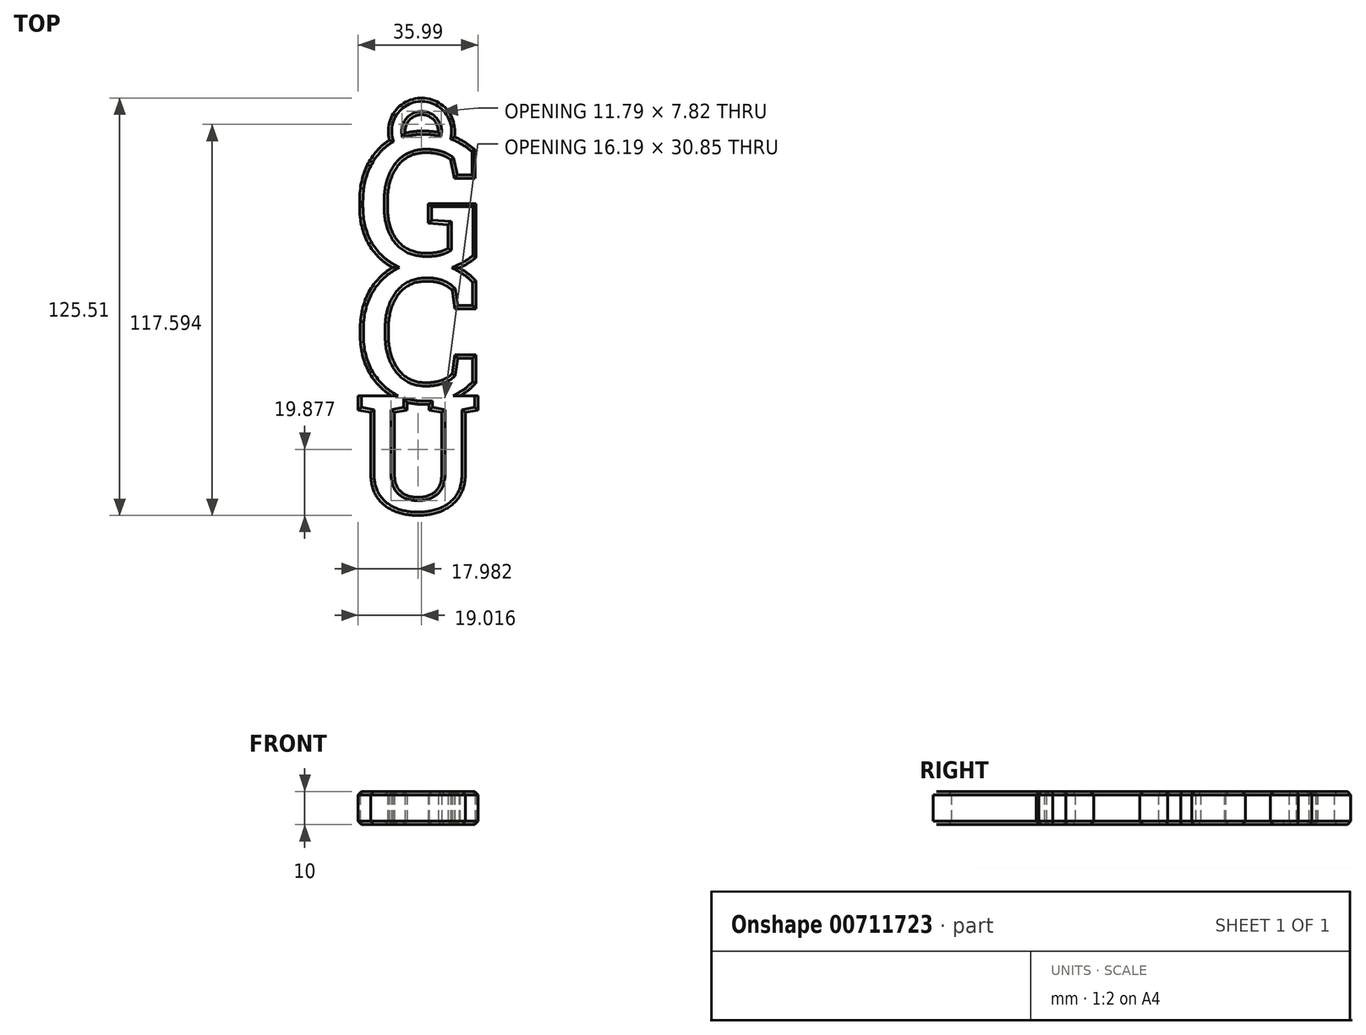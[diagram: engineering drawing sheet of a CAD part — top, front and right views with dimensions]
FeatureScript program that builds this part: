
annotation { "Feature Type Name" : "Feature", "Feature Type Description" : "" }
export const myFeature = defineFeature(function(context is Context, id is Id, definition is map)
    precondition{}
    {
        {
            var Q0;
            Q0=qCreatedBy(makeId("Top.planeOp"),FACE);
            var sketch = newSketch(context, id + "F0", { "sketchPlane" : qUnion([Q0])});
            skText(sketch, "E0", { "text": "G", "fontName": "RobotoSlab-Bold.ttf"});
            skText(sketch, "E1", { "text": "C", "fontName": "RobotoSlab-Bold.ttf"});
            skText(sketch, "E2", { "text": "U", "fontName": "RobotoSlab-Bold.ttf"});
            skCircle(sketch, "E3", {"center": v(0, 51.5) * mm, "radius": 10 * mm});
            skCircle(sketch, "E4", {"center": v(0, 51.5) * mm, "radius": 5 * mm});
            const initialGuessF0  = {"E0": [-0.02, 0.00902, 1, 0, 0.04248], "E1": [-0.02, -0.03003, 1, 0, 0.04292], "E2": [-0.02, -0.0635, 1, 0, 0.0359]};
            skSetInitialGuess(sketch, initialGuessF0);
            skSolve(sketch);
        }
        {
            var Q0;
            {var subQ11=sQuery(id+"F0.wireOp",EDGE,"E0.sketch_text.stroke-3");Q0=makeQuery(id+"F0.imprint","IMPRINT",FACE,{"disambiguationData":[TD([[makeQuery(id+"F0.imprint","IMPRINT",EDGE,{"derivedFrom":subQ11}),-1.0]])]});}
            var Q1;
            {var subQ7=sQuery(id+"F0.wireOp",EDGE,"E0.sketch_text.stroke-13");Q1=makeQuery(id+"F0.imprint","IMPRINT",FACE,{"disambiguationData":[TD([[makeQuery(id+"F0.imprint","IMPRINT",EDGE,{"derivedFrom":subQ7}),-1.0]])]});}
            var Q2;
            {var subQ0=sQuery(id+"F0.wireOp",EDGE,"E3");var subQ1=sQuery(id+"F0.wireOp",EDGE,"E0.sketch_text.stroke-6");var subQ2=makeQuery(id+"F0.imprint","INTERSECT",VERTEX,{"derivedFrom":[subQ1,subQ0]});Q2=makeQuery(id+"F0.imprint","IMPRINT",FACE,{"disambiguationData":[TD([[makeQuery(id+"F0.imprint","IMPRINT",EDGE,{"disambiguationData":[TD([[subQ2,-1.0]])],"derivedFrom":subQ1}),1.0]])]});}
            var Q3;
            {var subQ0=sQuery(id+"F0.wireOp",EDGE,"E0.sketch_text.stroke-7");var subQ1=sQuery(id+"F0.wireOp",EDGE,"E0.sketch_text.stroke-6");var subQ2=makeQuery(id+"F0.imprint","INTERSECT",VERTEX,{"derivedFrom":[subQ1,subQ0]});Q3=makeQuery(id+"F0.imprint","IMPRINT",FACE,{"disambiguationData":[TD([[makeQuery(id+"F0.imprint","IMPRINT",EDGE,{"disambiguationData":[TD([[subQ2,1.0]])],"derivedFrom":subQ1}),-1.0]])]});}
            var Q4;
            {var subQ6=sQuery(id+"F0.wireOp",EDGE,"E0.sketch_text.stroke-9");Q4=makeQuery(id+"F0.imprint","IMPRINT",FACE,{"disambiguationData":[TD([[makeQuery(id+"F0.imprint","IMPRINT",EDGE,{"derivedFrom":subQ6}),-1.0]])]});}
            var Q5;
            {var subQ4=sQuery(id+"F0.wireOp",EDGE,"E0.sketch_text.stroke-1");Q5=makeQuery(id+"F0.imprint","IMPRINT",FACE,{"disambiguationData":[TD([[makeQuery(id+"F0.imprint","IMPRINT",EDGE,{"derivedFrom":subQ4}),-1.0]])]});}
            var Q6;
            {var subQ12=sQuery(id+"F0.wireOp",EDGE,"E0.sketch_text.stroke-1");Q6=makeQuery(id+"F0.imprint","IMPRINT",FACE,{"disambiguationData":[TD([[makeQuery(id+"F0.imprint","IMPRINT",EDGE,{"derivedFrom":subQ12}),1.0]])]});}
            var Q7;
            {var subQ13=sQuery(id+"F0.wireOp",EDGE,"E2.sketch_text.stroke-1");Q7=makeQuery(id+"F0.imprint","IMPRINT",FACE,{"disambiguationData":[TD([[makeQuery(id+"F0.imprint","IMPRINT",EDGE,{"derivedFrom":subQ13}),-1.0]])]});}
            var Q8;
            {var subQ0=sQuery(id+"F0.wireOp",EDGE,"E1.sketch_text.stroke-15");var subQ1=sQuery(id+"F0.wireOp",EDGE,"E1.sketch_text.stroke-14");var subQ2=makeQuery(id+"F0.imprint","INTERSECT",VERTEX,{"derivedFrom":[subQ1,subQ0]});Q8=makeQuery(id+"F0.imprint","IMPRINT",FACE,{"disambiguationData":[TD([[makeQuery(id+"F0.imprint","IMPRINT",EDGE,{"disambiguationData":[TD([[subQ2,1.0]])],"derivedFrom":subQ1}),-1.0]])]});}
            var Q9;
            {var subQ5=sQuery(id+"F0.wireOp",EDGE,"E2.sketch_text.stroke-23");Q9=makeQuery(id+"F0.imprint","IMPRINT",FACE,{"disambiguationData":[TD([[makeQuery(id+"F0.imprint","IMPRINT",EDGE,{"derivedFrom":subQ5}),-1.0]])]});}
            extrude(context, id + "F1", {"entities" : qUnion([Q0, Q1, Q2, Q3, Q4, Q5, Q6, Q7, Q8, Q9]), "depth" : 10 * mm, "offsetDistance" : 25 * mm});
        }
        {
            var Q0;
            Q0=makeQuery(id+"F1.opExtrude","CAP_EDGE",EDGE,{"disambiguationData":[OSD([sQuery(id+"F0.wireOp",EDGE,"E0.sketch_text.stroke-2")])],"isStart":false});
            var Q1;
            Q1=makeQuery(id+"F1.opExtrude","CAP_EDGE",EDGE,{"disambiguationData":[OSD([sQuery(id+"F0.wireOp",EDGE,"E0.sketch_text.stroke-3")])],"isStart":false});
            var Q2;
            Q2=makeQuery(id+"F1.opExtrude","CAP_EDGE",EDGE,{"disambiguationData":[OSD([sQuery(id+"F0.wireOp",EDGE,"E3")])],"isStart":false});
            var Q3;
            Q3=makeQuery(id+"F1.opExtrude","CAP_EDGE",EDGE,{"disambiguationData":[OSD([sQuery(id+"F0.wireOp",EDGE,"E0.sketch_text.stroke-8")])],"isStart":false});
            var Q4;
            Q4=makeQuery(id+"F1.opExtrude","CAP_EDGE",EDGE,{"disambiguationData":[OSD([sQuery(id+"F0.wireOp",EDGE,"E0.sketch_text.stroke-9")])],"isStart":false});
            var Q5;
            Q5=makeQuery(id+"F1.opExtrude","CAP_EDGE",EDGE,{"disambiguationData":[OSD([sQuery(id+"F0.wireOp",EDGE,"E0.sketch_text.stroke-24")])],"isStart":false});
            var Q6;
            Q6=makeQuery(id+"F1.opExtrude","CAP_EDGE",EDGE,{"disambiguationData":[OSD([sQuery(id+"F0.wireOp",EDGE,"E0.sketch_text.stroke-10")])],"isStart":false});
            var Q7;
            Q7=makeQuery(id+"F1.opExtrude","CAP_EDGE",EDGE,{"disambiguationData":[OSD([sQuery(id+"F0.wireOp",EDGE,"E0.sketch_text.stroke-11")])],"isStart":false});
            var Q8;
            Q8=makeQuery(id+"F1.opExtrude","CAP_EDGE",EDGE,{"disambiguationData":[OSD([sQuery(id+"F0.wireOp",EDGE,"E0.sketch_text.stroke-13")])],"isStart":false});
            var Q9;
            Q9=makeQuery(id+"F1.opExtrude","CAP_EDGE",EDGE,{"disambiguationData":[OSD([sQuery(id+"F0.wireOp",EDGE,"E0.sketch_text.stroke-21")])],"isStart":false});
            var Q10;
            Q10=makeQuery(id+"F1.opExtrude","CAP_EDGE",EDGE,{"disambiguationData":[OSD([sQuery(id+"F0.wireOp",EDGE,"E0.sketch_text.stroke-22")])],"isStart":false});
            var Q11;
            Q11=makeQuery(id+"F1.opExtrude","CAP_EDGE",EDGE,{"disambiguationData":[OSD([sQuery(id+"F0.wireOp",EDGE,"E0.sketch_text.stroke-23")])],"isStart":false});
            var Q12;
            Q12=makeQuery(id+"F1.opExtrude","CAP_EDGE",EDGE,{"disambiguationData":[OSD([sQuery(id+"F0.wireOp",EDGE,"E0.sketch_text.stroke-25")])],"isStart":false});
            var Q13;
            Q13=makeQuery(id+"F1.opExtrude","CAP_EDGE",EDGE,{"disambiguationData":[OSD([sQuery(id+"F0.wireOp",EDGE,"E0.sketch_text.stroke-0")])],"isStart":false});
            var Q14;
            Q14=makeQuery(id+"F1.opExtrude","CAP_EDGE",EDGE,{"disambiguationData":[OSD([sQuery(id+"F0.wireOp",EDGE,"E1.sketch_text.stroke-22")])],"isStart":false});
            var Q15;
            Q15=makeQuery(id+"F1.opExtrude","CAP_EDGE",EDGE,{"disambiguationData":[OSD([sQuery(id+"F0.wireOp",EDGE,"E1.sketch_text.stroke-23")])],"isStart":false});
            var Q16;
            Q16=makeQuery(id+"F1.opExtrude","CAP_EDGE",EDGE,{"disambiguationData":[OSD([sQuery(id+"F0.wireOp",EDGE,"E1.sketch_text.stroke-0")])],"isStart":false});
            var Q17;
            Q17=makeQuery(id+"F1.opExtrude","CAP_EDGE",EDGE,{"disambiguationData":[OSD([sQuery(id+"F0.wireOp",EDGE,"E1.sketch_text.stroke-1")])],"isStart":false});
            var Q18;
            Q18=makeQuery(id+"F1.opExtrude","CAP_EDGE",EDGE,{"disambiguationData":[OSD([sQuery(id+"F0.wireOp",EDGE,"E1.sketch_text.stroke-2")])],"isStart":false});
            var Q19;
            Q19=makeQuery(id+"F1.opExtrude","CAP_EDGE",EDGE,{"disambiguationData":[OSD([sQuery(id+"F0.wireOp",EDGE,"E1.sketch_text.stroke-12")])],"isStart":false});
            var Q20;
            Q20=makeQuery(id+"F1.opExtrude","CAP_EDGE",EDGE,{"disambiguationData":[OSD([sQuery(id+"F0.wireOp",EDGE,"E1.sketch_text.stroke-11")])],"isStart":false});
            var Q21;
            Q21=makeQuery(id+"F1.opExtrude","CAP_EDGE",EDGE,{"disambiguationData":[OSD([sQuery(id+"F0.wireOp",EDGE,"E1.sketch_text.stroke-13")])],"isStart":false});
            var Q22;
            Q22=makeQuery(id+"F1.opExtrude","CAP_EDGE",EDGE,{"disambiguationData":[OSD([sQuery(id+"F0.wireOp",EDGE,"E1.sketch_text.stroke-14")])],"isStart":false});
            var Q23;
            Q23=makeQuery(id+"F1.opExtrude","CAP_EDGE",EDGE,{"disambiguationData":[OSD([sQuery(id+"F0.wireOp",EDGE,"E2.sketch_text.stroke-11")])],"isStart":false});
            var Q24;
            Q24=makeQuery(id+"F1.opExtrude","CAP_EDGE",EDGE,{"disambiguationData":[OSD([sQuery(id+"F0.wireOp",EDGE,"E2.sketch_text.stroke-12")])],"isStart":false});
            var Q25;
            Q25=makeQuery(id+"F1.opExtrude","CAP_EDGE",EDGE,{"disambiguationData":[OSD([sQuery(id+"F0.wireOp",EDGE,"E2.sketch_text.stroke-13")])],"isStart":false});
            var Q26;
            Q26=makeQuery(id+"F1.opExtrude","CAP_EDGE",EDGE,{"disambiguationData":[OSD([sQuery(id+"F0.wireOp",EDGE,"E1.sketch_text.stroke-17")])],"isStart":false});
            var Q27;
            Q27=makeQuery(id+"F1.opExtrude","CAP_EDGE",EDGE,{"disambiguationData":[OSD([sQuery(id+"F0.wireOp",EDGE,"E2.sketch_text.stroke-20")])],"isStart":false});
            var Q28;
            Q28=makeQuery(id+"F1.opExtrude","CAP_EDGE",EDGE,{"disambiguationData":[OSD([sQuery(id+"F0.wireOp",EDGE,"E2.sketch_text.stroke-19")])],"isStart":false});
            var Q29;
            Q29=makeQuery(id+"F1.opExtrude","CAP_EDGE",EDGE,{"disambiguationData":[OSD([sQuery(id+"F0.wireOp",EDGE,"E2.sketch_text.stroke-13")])],"isStart":true});
            var Q30;
            Q30=makeQuery(id+"F1.opExtrude","CAP_EDGE",EDGE,{"disambiguationData":[OSD([sQuery(id+"F0.wireOp",EDGE,"E2.sketch_text.stroke-7")])],"isStart":true});
            var Q31;
            Q31=makeQuery(id+"F1.opExtrude","CAP_EDGE",EDGE,{"disambiguationData":[OSD([sQuery(id+"F0.wireOp",EDGE,"E2.sketch_text.stroke-7")])],"isStart":false});
            var Q32;
            Q32=makeQuery(id+"F1.opExtrude","CAP_EDGE",EDGE,{"disambiguationData":[OSD([sQuery(id+"F0.wireOp",EDGE,"E2.sketch_text.stroke-8")])],"isStart":false});
            var Q33;
            {var subQ0=sQuery(id+"F0.wireOp",EDGE,"E1.sketch_text.stroke-16");Q33=makeQuery(id+"F1.opExtrude","CAP_EDGE",EDGE,{"disambiguationData":[OSD([subQ0]),TDD([makeQuery(id+"F0.imprint","IMPRINT",EDGE,{"disambiguationData":[TD([[makeQuery(id+"F0.imprint","INTERSECT",VERTEX,{"derivedFrom":[sQuery(id+"F0.wireOp",EDGE,"E1.sketch_text.stroke-15"),subQ0]}),-1.0]])],"derivedFrom":subQ0})])],"isStart":false});}
            var Q34;
            Q34=makeQuery(id+"F1.opExtrude","CAP_EDGE",EDGE,{"disambiguationData":[OSD([sQuery(id+"F0.wireOp",EDGE,"E2.sketch_text.stroke-1")])],"isStart":false});
            var Q35;
            Q35=makeQuery(id+"F1.opExtrude","CAP_EDGE",EDGE,{"disambiguationData":[OSD([sQuery(id+"F0.wireOp",EDGE,"E2.sketch_text.stroke-8")])],"isStart":true});
            var Q36;
            {var subQ0=sQuery(id+"F0.wireOp",EDGE,"E1.sketch_text.stroke-16");Q36=makeQuery(id+"F1.opExtrude","CAP_EDGE",EDGE,{"disambiguationData":[OSD([subQ0]),TDD([makeQuery(id+"F0.imprint","IMPRINT",EDGE,{"disambiguationData":[TD([[makeQuery(id+"F0.imprint","INTERSECT",VERTEX,{"derivedFrom":[sQuery(id+"F0.wireOp",EDGE,"E1.sketch_text.stroke-15"),subQ0]}),-1.0]])],"derivedFrom":subQ0})])],"isStart":true});}
            var Q37;
            Q37=makeQuery(id+"F1.opExtrude","CAP_EDGE",EDGE,{"disambiguationData":[OSD([sQuery(id+"F0.wireOp",EDGE,"E1.sketch_text.stroke-8")])],"isStart":true});
            var Q38;
            Q38=makeQuery(id+"F1.opExtrude","CAP_EDGE",EDGE,{"disambiguationData":[OSD([sQuery(id+"F0.wireOp",EDGE,"E2.sketch_text.stroke-12")])],"isStart":true});
            var Q39;
            Q39=makeQuery(id+"F1.opExtrude","CAP_EDGE",EDGE,{"disambiguationData":[OSD([sQuery(id+"F0.wireOp",EDGE,"E2.sketch_text.stroke-11")])],"isStart":true});
            var Q40;
            Q40=makeQuery(id+"F1.opExtrude","CAP_EDGE",EDGE,{"disambiguationData":[OSD([sQuery(id+"F0.wireOp",EDGE,"E2.sketch_text.stroke-19")])],"isStart":true});
            var Q41;
            Q41=makeQuery(id+"F1.opExtrude","CAP_EDGE",EDGE,{"disambiguationData":[OSD([sQuery(id+"F0.wireOp",EDGE,"E2.sketch_text.stroke-20")])],"isStart":true});
            var Q42;
            Q42=makeQuery(id+"F1.opExtrude","CAP_EDGE",EDGE,{"disambiguationData":[OSD([sQuery(id+"F0.wireOp",EDGE,"E1.sketch_text.stroke-17")])],"isStart":true});
            var Q43;
            Q43=makeQuery(id+"F1.opExtrude","CAP_EDGE",EDGE,{"disambiguationData":[OSD([sQuery(id+"F0.wireOp",EDGE,"E1.sketch_text.stroke-11")])],"isStart":true});
            var Q44;
            Q44=makeQuery(id+"F1.opExtrude","CAP_EDGE",EDGE,{"disambiguationData":[OSD([sQuery(id+"F0.wireOp",EDGE,"E1.sketch_text.stroke-12")])],"isStart":true});
            var Q45;
            Q45=makeQuery(id+"F1.opExtrude","CAP_EDGE",EDGE,{"disambiguationData":[OSD([sQuery(id+"F0.wireOp",EDGE,"E1.sketch_text.stroke-13")])],"isStart":true});
            var Q46;
            Q46=makeQuery(id+"F1.opExtrude","CAP_EDGE",EDGE,{"disambiguationData":[OSD([sQuery(id+"F0.wireOp",EDGE,"E1.sketch_text.stroke-14")])],"isStart":true});
            var Q47;
            Q47=makeQuery(id+"F1.opExtrude","CAP_EDGE",EDGE,{"disambiguationData":[OSD([sQuery(id+"F0.wireOp",EDGE,"E1.sketch_text.stroke-23")])],"isStart":true});
            var Q48;
            Q48=makeQuery(id+"F1.opExtrude","CAP_EDGE",EDGE,{"disambiguationData":[OSD([sQuery(id+"F0.wireOp",EDGE,"E1.sketch_text.stroke-0")])],"isStart":true});
            var Q49;
            Q49=makeQuery(id+"F1.opExtrude","CAP_EDGE",EDGE,{"disambiguationData":[OSD([sQuery(id+"F0.wireOp",EDGE,"E1.sketch_text.stroke-22")])],"isStart":true});
            var Q50;
            Q50=makeQuery(id+"F1.opExtrude","CAP_EDGE",EDGE,{"disambiguationData":[OSD([sQuery(id+"F0.wireOp",EDGE,"E0.sketch_text.stroke-0")])],"isStart":true});
            var Q51;
            Q51=makeQuery(id+"F1.opExtrude","CAP_EDGE",EDGE,{"disambiguationData":[OSD([sQuery(id+"F0.wireOp",EDGE,"E0.sketch_text.stroke-25")])],"isStart":true});
            var Q52;
            Q52=makeQuery(id+"F1.opExtrude","CAP_EDGE",EDGE,{"disambiguationData":[OSD([sQuery(id+"F0.wireOp",EDGE,"E0.sketch_text.stroke-24")])],"isStart":true});
            var Q53;
            Q53=makeQuery(id+"F1.opExtrude","CAP_EDGE",EDGE,{"disambiguationData":[OSD([sQuery(id+"F0.wireOp",EDGE,"E0.sketch_text.stroke-22")])],"isStart":true});
            var Q54;
            Q54=makeQuery(id+"F1.opExtrude","CAP_EDGE",EDGE,{"disambiguationData":[OSD([sQuery(id+"F0.wireOp",EDGE,"E0.sketch_text.stroke-21")])],"isStart":true});
            var Q55;
            Q55=makeQuery(id+"F1.opExtrude","CAP_EDGE",EDGE,{"disambiguationData":[OSD([sQuery(id+"F0.wireOp",EDGE,"E0.sketch_text.stroke-17")])],"isStart":true});
            var Q56;
            Q56=makeQuery(id+"F1.opExtrude","CAP_EDGE",EDGE,{"disambiguationData":[OSD([sQuery(id+"F0.wireOp",EDGE,"E3")])],"isStart":true});
            var Q57;
            Q57=makeQuery(id+"F1.opExtrude","CAP_EDGE",EDGE,{"disambiguationData":[OSD([sQuery(id+"F0.wireOp",EDGE,"E4")])],"isStart":true});
            var Q58;
            Q58=makeQuery(id+"F1.opExtrude","CAP_EDGE",EDGE,{"disambiguationData":[OSD([sQuery(id+"F0.wireOp",EDGE,"E0.sketch_text.stroke-7")])],"isStart":true});
            var Q59;
            Q59=makeQuery(id+"F1.opExtrude","CAP_EDGE",EDGE,{"disambiguationData":[OSD([sQuery(id+"F0.wireOp",EDGE,"E0.sketch_text.stroke-8")])],"isStart":true});
            var Q60;
            Q60=makeQuery(id+"F1.opExtrude","CAP_EDGE",EDGE,{"disambiguationData":[OSD([sQuery(id+"F0.wireOp",EDGE,"E0.sketch_text.stroke-9")])],"isStart":true});
            var Q61;
            Q61=makeQuery(id+"F1.opExtrude","CAP_EDGE",EDGE,{"disambiguationData":[OSD([sQuery(id+"F0.wireOp",EDGE,"E0.sketch_text.stroke-10")])],"isStart":true});
            var Q62;
            Q62=makeQuery(id+"F1.opExtrude","CAP_EDGE",EDGE,{"disambiguationData":[OSD([sQuery(id+"F0.wireOp",EDGE,"E0.sketch_text.stroke-11")])],"isStart":true});
            var Q63;
            {var subQ0=sQuery(id+"F0.wireOp",EDGE,"E0.sketch_text.stroke-6");Q63=makeQuery(id+"F1.opExtrude","CAP_EDGE",EDGE,{"disambiguationData":[OSD([subQ0]),TDD([makeQuery(id+"F0.imprint","IMPRINT",EDGE,{"disambiguationData":[TD([[makeQuery(id+"F0.imprint","INTERSECT",VERTEX,{"derivedFrom":[subQ0,sQuery(id+"F0.wireOp",EDGE,"E0.sketch_text.stroke-7")]}),1.0]])],"derivedFrom":subQ0})])],"isStart":false});}
            var Q64;
            Q64=makeQuery(id+"F1.opExtrude","CAP_EDGE",EDGE,{"disambiguationData":[OSD([sQuery(id+"F0.wireOp",EDGE,"E4")])],"isStart":false});
            var Q65;
            Q65=makeQuery(id+"F1.opExtrude","CAP_EDGE",EDGE,{"disambiguationData":[OSD([sQuery(id+"F0.wireOp",EDGE,"E0.sketch_text.stroke-5")])],"isStart":true});
            var Q66;
            Q66=makeQuery(id+"F1.opExtrude","CAP_EDGE",EDGE,{"disambiguationData":[OSD([sQuery(id+"F0.wireOp",EDGE,"E1.sketch_text.stroke-1")])],"isStart":true});
            var Q67;
            Q67=makeQuery(id+"F1.opExtrude","CAP_EDGE",EDGE,{"disambiguationData":[OSD([sQuery(id+"F0.wireOp",EDGE,"E2.sketch_text.stroke-1")])],"isStart":true});
            var Q68;
            Q68=makeQuery(id+"F1.opExtrude","CAP_EDGE",EDGE,{"disambiguationData":[OSD([sQuery(id+"F0.wireOp",EDGE,"E2.sketch_text.stroke-0")])],"isStart":true});
            var Q69;
            Q69=makeQuery(id+"F1.opExtrude","CAP_EDGE",EDGE,{"disambiguationData":[OSD([sQuery(id+"F0.wireOp",EDGE,"E2.sketch_text.stroke-9")])],"isStart":true});
            var Q70;
            Q70=makeQuery(id+"F1.opExtrude","CAP_EDGE",EDGE,{"disambiguationData":[OSD([sQuery(id+"F0.wireOp",EDGE,"E2.sketch_text.stroke-9")])],"isStart":false});
            var Q71;
            Q71=makeQuery(id+"F1.opExtrude","CAP_EDGE",EDGE,{"disambiguationData":[OSD([sQuery(id+"F0.wireOp",EDGE,"E2.sketch_text.stroke-0")])],"isStart":false});
            chamfer(context, id + "F2", {"entities" : qUnion([Q0, Q1, Q2, Q3, Q4, Q5, Q6, Q7, Q8, Q9, Q10, Q11, Q12, Q13, Q14, Q15, Q16, Q17, Q18, Q19, Q20, Q21, Q22, Q23, Q24, Q25, Q26, Q27, Q28, Q29, Q30, Q31, Q32, Q33, Q34, Q35, Q36, Q37, Q38, Q39, Q40, Q41, Q42, Q43, Q44, Q45, Q46, Q47, Q48, Q49, Q50, Q51, Q52, Q53, Q54, Q55, Q56, Q57, Q58, Q59, Q60, Q61, Q62, Q63, Q64, Q65, Q66, Q67, Q68, Q69, Q70, Q71]), "width" : 1 * mm, "tangentPropagation" : true});
        }
    });
